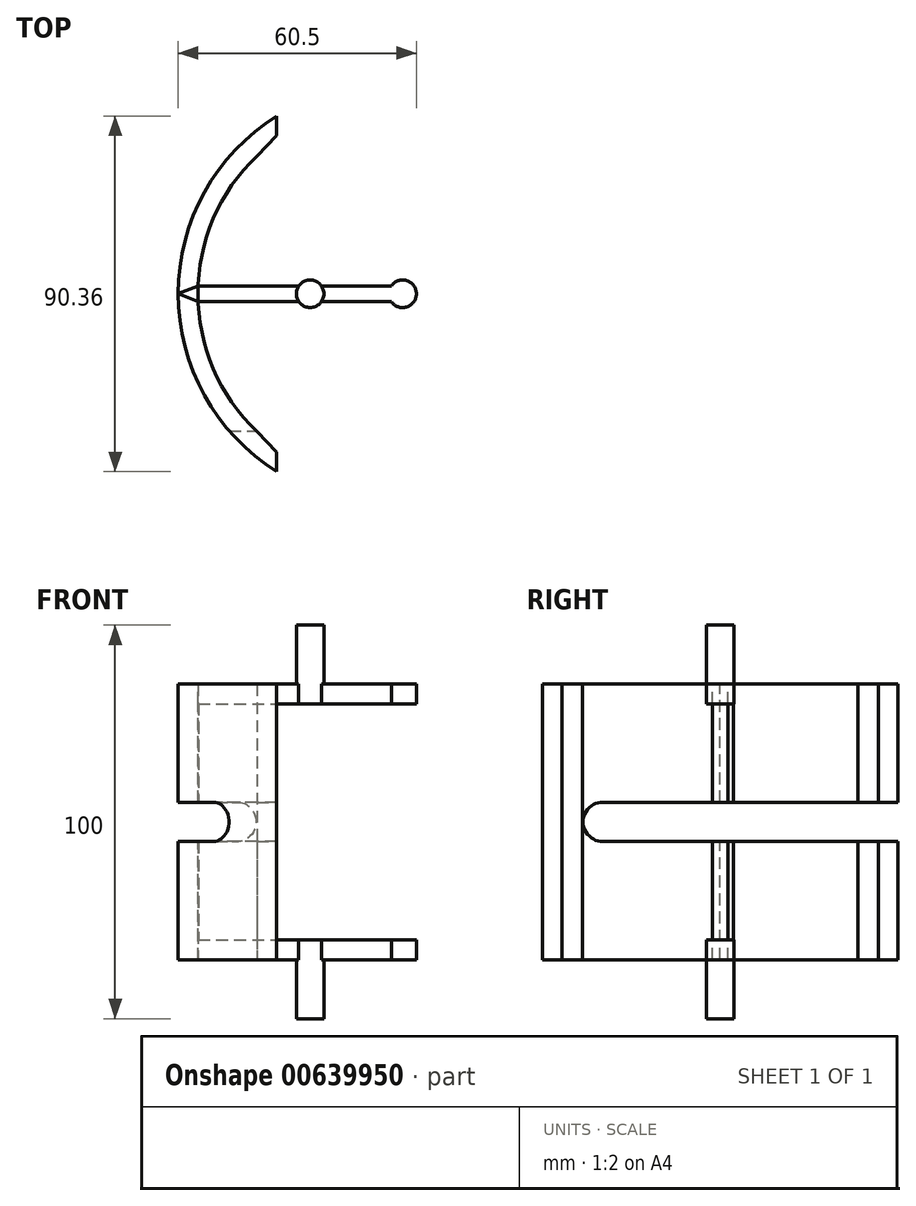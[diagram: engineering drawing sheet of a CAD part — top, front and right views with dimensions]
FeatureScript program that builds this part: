
annotation { "Feature Type Name" : "Feature", "Feature Type Description" : "" }
export const myFeature = defineFeature(function(context is Context, id is Id, definition is map)
    precondition{}
    {
        {
            var Q0;
            Q0=qCreatedBy(makeId("Top.planeOp"),FACE);
            var sketch = newSketch(context, id + "F0", { "sketchPlane" : qUnion([Q0])});
            skPoint(sketch, "E0", {"position": v(0, 35) * mm});
            skArc(sketch, "E1", {"start": v(0, 70) * mm, "mid": v(-15, 35) * mm, "end": v(0, 0) * mm});
            skArc(sketch, "E2.0", {"start": v(5, 80.18) * mm, "mid": v(-20, 35) * mm, "end": v(5, -10.18) * mm});
            skPoint(sketch, "E3", {"position": v(5, 75.18) * mm});
            skPoint(sketch, "E4", {"position": v(5, -5.18) * mm});
            skLineSegment(sketch, "E5", {"start": v(0, 0) * mm, "end": v(5, -5.18) * mm});
            skLineSegment(sketch, "E6", {"start": v(0, 70) * mm, "end": v(5, 75.18) * mm});
            skLineSegment(sketch, "E7", {"start": v(5, 80.18) * mm, "end": v(5, 75.18) * mm});
            skLineSegment(sketch, "E8", {"start": v(5, -10.18) * mm, "end": v(5, -5.18) * mm});
            skSolve(sketch);
        }
        {
            var Q0;
            Q0=makeQuery(id+"F0.imprint","IMPRINT",FACE,{"disambiguationData":[TD([[makeQuery(id+"F0.imprint","IMPRINT",EDGE,{"derivedFrom":sQuery(id+"F0.wireOp",EDGE,"E1")}),-1.0]])]});
            extrude(context, id + "F1", {"entities" : qUnion([Q0]), "depth" : 70 * mm, "offsetDistance" : 25 * mm});
        }
        {
            var Q0;
            Q0=makeQuery(id+"F1.opExtrude","SWEPT_FACE",FACE,{"disambiguationData":[OSD([sQuery(id+"F0.wireOp",EDGE,"E7")])]});
            var sketch = newSketch(context, id + "F2", { "sketchPlane" : qUnion([Q0])});
            skPoint(sketch, "E9", {"position": v(80.18, 40) * mm});
            skPoint(sketch, "E10", {"position": v(80.18, 30) * mm});
            skLineSegment(sketch, "E11", {"start": v(80.18, 40) * mm, "end": v(5.18, 40) * mm});
            skLineSegment(sketch, "E12", {"start": v(80.18, 30) * mm, "end": v(5.18, 30) * mm});
            skArc(sketch, "E13", {"start": v(5.18, 40) * mm, "mid": v(0.18, 35) * mm, "end": v(5.18, 30) * mm});
            skSolve(sketch);
        }
        {
            var Q0;
            Q0 = qSketchRegion(id + "F2", true);
            var Q1;
            {var subQ0=sQuery(id+"F2.wireOp",EDGE,"E13");Q1=makeQuery(id+"F2.imprint","IMPRINT",FACE,{"disambiguationData":[TD([[makeQuery(id+"F2.imprint","IMPRINT",EDGE,{"derivedFrom":subQ0}),1.0]])]});}
            extrude(context, id + "F3", {"entities" : qUnion([Q0, Q1]), "operationType" : NewBodyOperationType.REMOVE, "oppositeDirection" : true, "depth" : 34.1 * mm, "offsetDistance" : 25 * mm});
        }
        {
            var Q0;
            Q0=makeQuery(id+"F3.boolean.opBoolean","COPY",FACE,{"derivedFrom":makeQuery(id+"F3.opExtrude","SWEPT_FACE",FACE,{"disambiguationData":[OSD([sQuery(id+"F0.wireOp",EDGE,"E6"),sQuery(id+"F0.wireOp",EDGE,"E7")])]})});
            extrude(context, id + "F4", {"entities" : qUnion([Q0]), "operationType" : NewBodyOperationType.REMOVE, "oppositeDirection" : true, "depth" : 25 * mm, "offsetDistance" : 25 * mm});
        }
        {
            var Q0;
            Q0=makeQuery(id+"F1.opExtrude","CAP_FACE",FACE,{"disambiguationData":[OSD([sQuery(id+"F0.wireOp",EDGE,"E1"),sQuery(id+"F0.wireOp",EDGE,"E2.0"),sQuery(id+"F0.wireOp",EDGE,"E5"),sQuery(id+"F0.wireOp",EDGE,"E6"),sQuery(id+"F0.wireOp",EDGE,"E7"),sQuery(id+"F0.wireOp",EDGE,"E8")])],"isStart":false});
            var sketch = newSketch(context, id + "F5", { "sketchPlane" : qUnion([Q0])});
            skLineSegment(sketch, "E14", {"start": v(5, 35) * mm, "end": v(-20, 35) * mm});
            skLineSegment(sketch, "E15", {"start": v(-20, 35) * mm, "end": v(10, 35) * mm});
            skLineSegment(sketch, "E16", {"start": v(10, 35) * mm, "end": v(17, 35) * mm});
            skLineSegment(sketch, "E17", {"start": v(17, 35) * mm, "end": v(37, 35) * mm});
            skPoint(sketch, "E18", {"position": v(13.5, 35) * mm});
            skCircle(sketch, "E19", {"center": v(13.5, 35) * mm, "radius": 3.5 * mm});
            skPoint(sketch, "E20", {"position": v(-14.96, 37) * mm});
            skPoint(sketch, "E21", {"position": v(-14.96, 33) * mm});
            skLineSegment(sketch, "E22", {"start": v(-20, 35) * mm, "end": v(-14.96, 37) * mm});
            skLineSegment(sketch, "E23", {"start": v(-14.96, 33) * mm, "end": v(-20, 35) * mm});
            skLineSegment(sketch, "E24", {"start": v(-14.96, 33) * mm, "end": v(10.63, 33) * mm});
            skLineSegment(sketch, "E25", {"start": v(-14.96, 37) * mm, "end": v(10.63, 37) * mm});
            skLineSegment(sketch, "E26", {"start": v(10.63, 37) * mm, "end": v(16.37, 37) * mm});
            skLineSegment(sketch, "E27", {"start": v(10.63, 33) * mm, "end": v(16.37, 33) * mm});
            skLineSegment(sketch, "E28", {"start": v(37, 35) * mm, "end": v(37, 37) * mm});
            skLineSegment(sketch, "E29", {"start": v(37, 35) * mm, "end": v(37, 33) * mm});
            skLineSegment(sketch, "E30", {"start": v(37, 33) * mm, "end": v(16.37, 33) * mm});
            skLineSegment(sketch, "E31", {"start": v(16.37, 37) * mm, "end": v(37, 37) * mm});
            skPoint(sketch, "E32", {"position": v(33.5, 35) * mm});
            skCircle(sketch, "E33", {"center": v(37, 35) * mm, "radius": 3.5 * mm});
            skPoint(sketch, "E34", {"position": v(-15, 35) * mm});
            skSolve(sketch);
        }
        {
            var Q0;
            Q0 = qSketchRegion(id + "F5", true);
            extrude(context, id + "F6", {"entities" : qUnion([Q0]), "oppositeDirection" : true, "depth" : 70 * mm, "offsetDistance" : 25 * mm});
        }
        {
            var Q0;
            Q0=makeQuery(id+"F6.opExtrude","SWEPT_FACE",FACE,{"disambiguationData":[OSD([sQuery(id+"F5.wireOp",EDGE,"E24")])]});
            var sketch = newSketch(context, id + "F7", { "sketchPlane" : qUnion([Q0])});
            skPoint(sketch, "E35", {"position": v(-14.96, 65) * mm});
            skPoint(sketch, "E36", {"position": v(-14.96, 5) * mm});
            skLineSegment(sketch, "E37", {"start": v(-14.96, 5) * mm, "end": v(103.18, 5) * mm});
            skLineSegment(sketch, "E38.bottom", {"start": v(-14.96, 65) * mm, "end": v(84.94, 65) * mm});
            skLineSegment(sketch, "E38.top", {"start": v(-14.96, 5) * mm, "end": v(84.94, 5) * mm});
            skLineSegment(sketch, "E38.left", {"start": v(-14.96, 65) * mm, "end": v(-14.96, 5) * mm});
            skLineSegment(sketch, "E38.right", {"start": v(84.94, 65) * mm, "end": v(84.94, 5) * mm});
            skSolve(sketch);
        }
        {
            var Q0;
            Q0 = qSketchRegion(id + "F7", true);
            extrude(context, id + "F8", {"entities" : qUnion([Q0]), "operationType" : NewBodyOperationType.REMOVE, "oppositeDirection" : true, "depth" : 5.4 * mm, "offsetDistance" : 25 * mm});
        }
        {
            var Q0;
            {var subQ0=sQuery(id+"F7.wireOp",EDGE,"E38.bottom");var subQ1=sQuery(id+"F7.wireOp",EDGE,"E38.top");Q0=makeQuery(id+"F8.boolean.opBoolean","COPY",FACE,{"disambiguationData":[TD([makeQuery(id+"F6.opExtrude","SWEPT_FACE",FACE,{"disambiguationData":[OSD([sQuery(id+"F5.wireOp",EDGE,"E33")])]})])],"derivedFrom":makeQuery(id+"F8.opExtrude","CAP_FACE",FACE,{"disambiguationData":[OSD([subQ0,subQ1,sQuery(id+"F7.wireOp",EDGE,"E38.left"),sQuery(id+"F7.wireOp",EDGE,"E38.right")])],"isStart":true})});}
            extrude(context, id + "F9", {"entities" : qUnion([Q0]), "operationType" : NewBodyOperationType.REMOVE, "oppositeDirection" : true, "depth" : 25 * mm, "offsetDistance" : 25 * mm});
        }
        {
            var Q0;
            {var subQ0=sQuery(id+"F5.wireOp",EDGE,"E24");var subQ1=sQuery(id+"F7.wireOp",EDGE,"E38.bottom");var subQ5=sQuery(id+"F7.wireOp",EDGE,"E38.top");Q0=makeQuery(id+"F8.boolean.opBoolean","COPY",FACE,{"disambiguationData":[TD([makeQuery(id+"F6.opExtrude","SWEPT_FACE",FACE,{"disambiguationData":[OSD([subQ0])]})])],"derivedFrom":makeQuery(id+"F8.opExtrude","CAP_FACE",FACE,{"disambiguationData":[OSD([subQ1,subQ5,sQuery(id+"F7.wireOp",EDGE,"E38.left"),sQuery(id+"F7.wireOp",EDGE,"E38.right")])],"isStart":true})});}
            extrude(context, id + "F10", {"entities" : qUnion([Q0]), "operationType" : NewBodyOperationType.REMOVE, "oppositeDirection" : true, "depth" : 25 * mm, "offsetDistance" : 25 * mm});
        }
        {
            var Q0;
            {var subQ0=sQuery(id+"F7.wireOp",EDGE,"E38.bottom");var subQ1=sQuery(id+"F7.wireOp",EDGE,"E38.top");Q0=makeQuery(id+"F8.boolean.opBoolean","COPY",FACE,{"disambiguationData":[TD([makeQuery(id+"F6.opExtrude","SWEPT_FACE",FACE,{"disambiguationData":[OSD([sQuery(id+"F5.wireOp",EDGE,"E33")])]})])],"derivedFrom":makeQuery(id+"F8.opExtrude","CAP_FACE",FACE,{"disambiguationData":[OSD([subQ0,subQ1,sQuery(id+"F7.wireOp",EDGE,"E38.left"),sQuery(id+"F7.wireOp",EDGE,"E38.right")])],"isStart":false})});}
            extrude(context, id + "F11", {"entities" : qUnion([Q0]), "operationType" : NewBodyOperationType.REMOVE, "oppositeDirection" : true, "depth" : 25 * mm, "offsetDistance" : 25 * mm});
        }
        {
            var Q0;
            {var subQ0=sQuery(id+"F5.wireOp",EDGE,"E26");var subQ1=sQuery(id+"F5.wireOp",EDGE,"E19");var subQ2=sQuery(id+"F7.wireOp",EDGE,"E38.bottom");var subQ3=sQuery(id+"F7.wireOp",EDGE,"E38.top");Q0=makeQuery(id+"F8.boolean.opBoolean","COPY",FACE,{"disambiguationData":[TD([makeQuery(id+"F6.opExtrude","SWEPT_FACE",FACE,{"disambiguationData":[OSD([subQ1]),TDD([makeQuery(id+"F5.imprint","IMPRINT",EDGE,{"disambiguationData":[TD([[makeQuery(id+"F5.imprint","INTERSECT",VERTEX,{"derivedFrom":[subQ1,sQuery(id+"F5.wireOp",EDGE,"E25"),subQ0]}),1.0]])],"derivedFrom":subQ1})])]})])],"derivedFrom":makeQuery(id+"F8.opExtrude","CAP_FACE",FACE,{"disambiguationData":[OSD([subQ2,subQ3,sQuery(id+"F7.wireOp",EDGE,"E38.left"),sQuery(id+"F7.wireOp",EDGE,"E38.right")])],"isStart":false})});}
            extrude(context, id + "F12", {"entities" : qUnion([Q0]), "operationType" : NewBodyOperationType.REMOVE, "oppositeDirection" : true, "depth" : 25 * mm, "offsetDistance" : 25 * mm});
        }
        {
            var Q0;
            Q0=makeQuery(id+"F8.boolean.opBoolean","COPY",FACE,{"derivedFrom":makeQuery(id+"F8.opExtrude","SWEPT_FACE",FACE,{"disambiguationData":[OSD([sQuery(id+"F7.wireOp",EDGE,"E38.left")])]})});
            var sketch = newSketch(context, id + "F13", { "sketchPlane" : qUnion([Q0])});
            skLineSegment(sketch, "E39.bottom", {"start": v(33, 39.94) * mm, "end": v(37, 39.94) * mm});
            skLineSegment(sketch, "E39.top", {"start": v(33, 30.02) * mm, "end": v(37, 30.02) * mm});
            skLineSegment(sketch, "E39.left", {"start": v(33, 39.94) * mm, "end": v(33, 30.02) * mm});
            skLineSegment(sketch, "E39.right", {"start": v(37, 39.94) * mm, "end": v(37, 30.02) * mm});
            skSolve(sketch);
        }
        {
            var Q0;
            Q0 = qSketchRegion(id + "F13", true);
            extrude(context, id + "F14", {"entities" : qUnion([Q0]), "operationType" : NewBodyOperationType.REMOVE, "oppositeDirection" : true, "depth" : 25 * mm, "offsetDistance" : 25 * mm});
        }
        {
            var Q0;
            Q0=makeQuery(id+"F6.opExtrude","CAP_FACE",FACE,{"disambiguationData":[OSD([sQuery(id+"F5.wireOp",EDGE,"E19"),sQuery(id+"F5.wireOp",EDGE,"E22"),sQuery(id+"F5.wireOp",EDGE,"E23"),sQuery(id+"F5.wireOp",EDGE,"E24"),sQuery(id+"F5.wireOp",EDGE,"E25"),sQuery(id+"F5.wireOp",EDGE,"E30"),sQuery(id+"F5.wireOp",EDGE,"E31"),sQuery(id+"F5.wireOp",EDGE,"E33")])],"isStart":false});
            var sketch = newSketch(context, id + "F15", { "sketchPlane" : qUnion([Q0])});
            skCircle(sketch, "E40", {"center": v(13.5, -35) * mm, "radius": 3.5 * mm});
            skPoint(sketch, "E40.first.point", {"position": v(16.37, -33) * mm});
            skPoint(sketch, "E40.second.point", {"position": v(10.63, -37) * mm});
            skPoint(sketch, "E40.third.point", {"position": v(11.05, -32.5) * mm});
            skSolve(sketch);
        }
        {
            var Q0;
            {var subQ0=sQuery(id+"F15.wireOp",EDGE,"E40");var subQ1=makeQuery(id+"F15.imprint","INTERSECT",VERTEX,{"derivedFrom":[makeQuery(id+"F6.opExtrude","CAP_EDGE",EDGE,{"disambiguationData":[OSD([sQuery(id+"F5.wireOp",EDGE,"E25")])],"isStart":false}),subQ0]});var subQ2=makeQuery(id+"F15.imprint","INTERSECT",VERTEX,{"derivedFrom":[makeQuery(id+"F6.opExtrude","CAP_EDGE",EDGE,{"disambiguationData":[OSD([sQuery(id+"F5.wireOp",EDGE,"E31")])],"isStart":false}),subQ0]});Q0=makeQuery(id+"F15.imprint","IMPRINT",FACE,{"disambiguationData":[TD([[makeQuery(id+"F15.imprint","IMPRINT",EDGE,{"disambiguationData":[TD([[subQ1,1.0],[subQ2,-1.0]])],"derivedFrom":subQ0}),-1.0]])]});}
            extrude(context, id + "F16", {"entities" : qUnion([Q0]), "operationType" : NewBodyOperationType.ADD, "depth" : 15 * mm, "offsetDistance" : 25 * mm});
        }
        {
            var Q0;
            Q0=makeQuery(id+"F6.opExtrude","CAP_FACE",FACE,{"disambiguationData":[OSD([sQuery(id+"F5.wireOp",EDGE,"E19"),sQuery(id+"F5.wireOp",EDGE,"E22"),sQuery(id+"F5.wireOp",EDGE,"E23"),sQuery(id+"F5.wireOp",EDGE,"E24"),sQuery(id+"F5.wireOp",EDGE,"E25"),sQuery(id+"F5.wireOp",EDGE,"E30"),sQuery(id+"F5.wireOp",EDGE,"E31"),sQuery(id+"F5.wireOp",EDGE,"E33")])],"isStart":true});
            var sketch = newSketch(context, id + "F17", { "sketchPlane" : qUnion([Q0])});
            skCircle(sketch, "E41", {"center": v(13.5, 35) * mm, "radius": 3.5 * mm});
            skPoint(sketch, "E41.first.point", {"position": v(10.63, 37) * mm});
            skPoint(sketch, "E41.second.point", {"position": v(16.37, 33) * mm});
            skPoint(sketch, "E41.third.point", {"position": v(16, 32.54) * mm});
            skSolve(sketch);
        }
        {
            var Q0;
            {var subQ0=sQuery(id+"F17.wireOp",EDGE,"E41");var subQ1=makeQuery(id+"F17.imprint","INTERSECT",VERTEX,{"derivedFrom":[makeQuery(id+"F6.opExtrude","CAP_EDGE",EDGE,{"disambiguationData":[OSD([sQuery(id+"F5.wireOp",EDGE,"E25")])],"isStart":true}),subQ0]});Q0=makeQuery(id+"F17.imprint","IMPRINT",FACE,{"disambiguationData":[TD([[makeQuery(id+"F17.imprint","IMPRINT",EDGE,{"disambiguationData":[TD([[subQ1,1.0]])],"derivedFrom":subQ0}),1.0]])]});}
            extrude(context, id + "F18", {"entities" : qUnion([Q0]), "operationType" : NewBodyOperationType.ADD, "depth" : 15 * mm, "offsetDistance" : 25 * mm});
        }
    });
